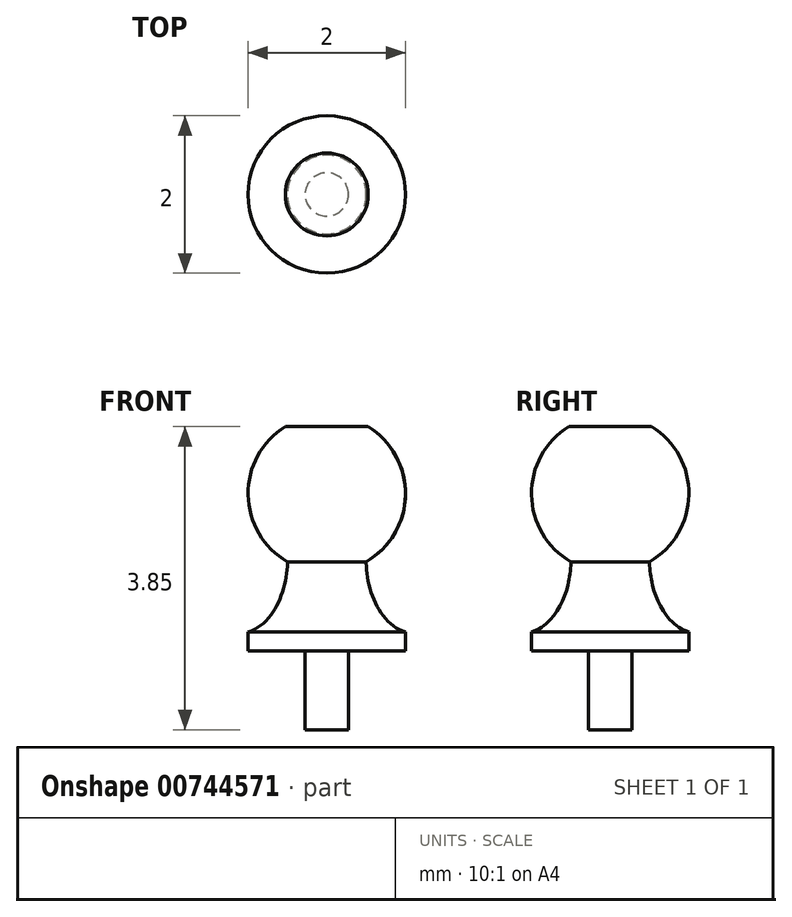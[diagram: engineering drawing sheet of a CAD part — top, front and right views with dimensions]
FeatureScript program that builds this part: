
annotation { "Feature Type Name" : "Feature", "Feature Type Description" : "" }
export const myFeature = defineFeature(function(context is Context, id is Id, definition is map)
    precondition{}
    {
        {
            var Q0;
            Q0=qCreatedBy(makeId("Front.planeOp"),FACE);
            var sketch = newSketch(context, id + "F0", { "sketchPlane" : qUnion([Q0])});
            skArc(sketch, "E0", {"start": v(-0.53, 0.85) * mm, "mid": v(-0.96, -0.27) * mm, "end": v(0, -1) * mm});
            skLineSegment(sketch, "E1", {"start": v(0, -1) * mm, "end": v(0, 0.85) * mm});
            skLineSegment(sketch, "E2", {"start": v(0, 0.85) * mm, "end": v(-0.53, 0.85) * mm});
            skPoint(sketch, "E3.orphan", {"position": v(0, -1.16) * mm});
            skLineSegment(sketch, "E4", {"start": v(-1, -2) * mm, "end": v(-1, -1.76) * mm});
            skLineSegment(sketch, "E5", {"start": v(-1, -2) * mm, "end": v(0, -2) * mm});
            skPoint(sketch, "E6.start.orphan", {"position": v(0, -0.08) * mm});
            skLineSegment(sketch, "E7", {"start": v(-0.5, -0.87) * mm, "end": v(-0.5, -0.88) * mm});
            skLineSegment(sketch, "E8", {"start": v(-0.5, -1.62) * mm, "end": v(-0.5, -1.62) * mm});
            skFitSpline(sketch, "E9", {"points": [v(-1, -1.76) * mm, v(-0.5, -0.87) * mm], "startDerivative": vector(0.98, 0.27) * mm, "endDerivative": vector(0, 1.02) * mm});
            skLineSegment(sketch, "E10", {"start": v(0, -1) * mm, "end": v(0, -2) * mm});
            skLineSegment(sketch, "E11", {"start": v(0, -2) * mm, "end": v(0, -3) * mm});
            skLineSegment(sketch, "E12", {"start": v(0, -3) * mm, "end": v(-0.28, -3) * mm});
            skLineSegment(sketch, "E13", {"start": v(-0.28, -3) * mm, "end": v(-0.28, -2) * mm});
            skSolve(sketch);
        }
        {
            var Q0;
            {var subQ0=sQuery(id+"F0.wireOp",EDGE,"E4");Q0=makeQuery(id+"F0.imprint","IMPRINT",FACE,{"disambiguationData":[TD([[makeQuery(id+"F0.imprint","IMPRINT",EDGE,{"derivedFrom":subQ0}),-1.0]])]});}
            var Q1;
            {var subQ3=sQuery(id+"F0.wireOp",EDGE,"E1");Q1=makeQuery(id+"F0.imprint","IMPRINT",FACE,{"disambiguationData":[TD([[makeQuery(id+"F0.imprint","IMPRINT",EDGE,{"derivedFrom":subQ3}),1.0]])]});}
            var Q2;
            {var subQ0=sQuery(id+"F0.wireOp",EDGE,"E11");Q2=makeQuery(id+"F0.imprint","IMPRINT",FACE,{"disambiguationData":[TD([[makeQuery(id+"F0.imprint","IMPRINT",EDGE,{"derivedFrom":subQ0}),-1.0]])]});}
            var Q3;
            Q3=sQuery(id+"F0.wireOp",EDGE,"E10");
            revolve(context, id + "F1", {"surfaceOperationType" : NewSurfaceOperationType.NEW, "entities" : qUnion([Q0, Q1, Q2]), "axis" : qUnion([Q3]), "revolveType" : RevolveType.FULL});
        }
    });
